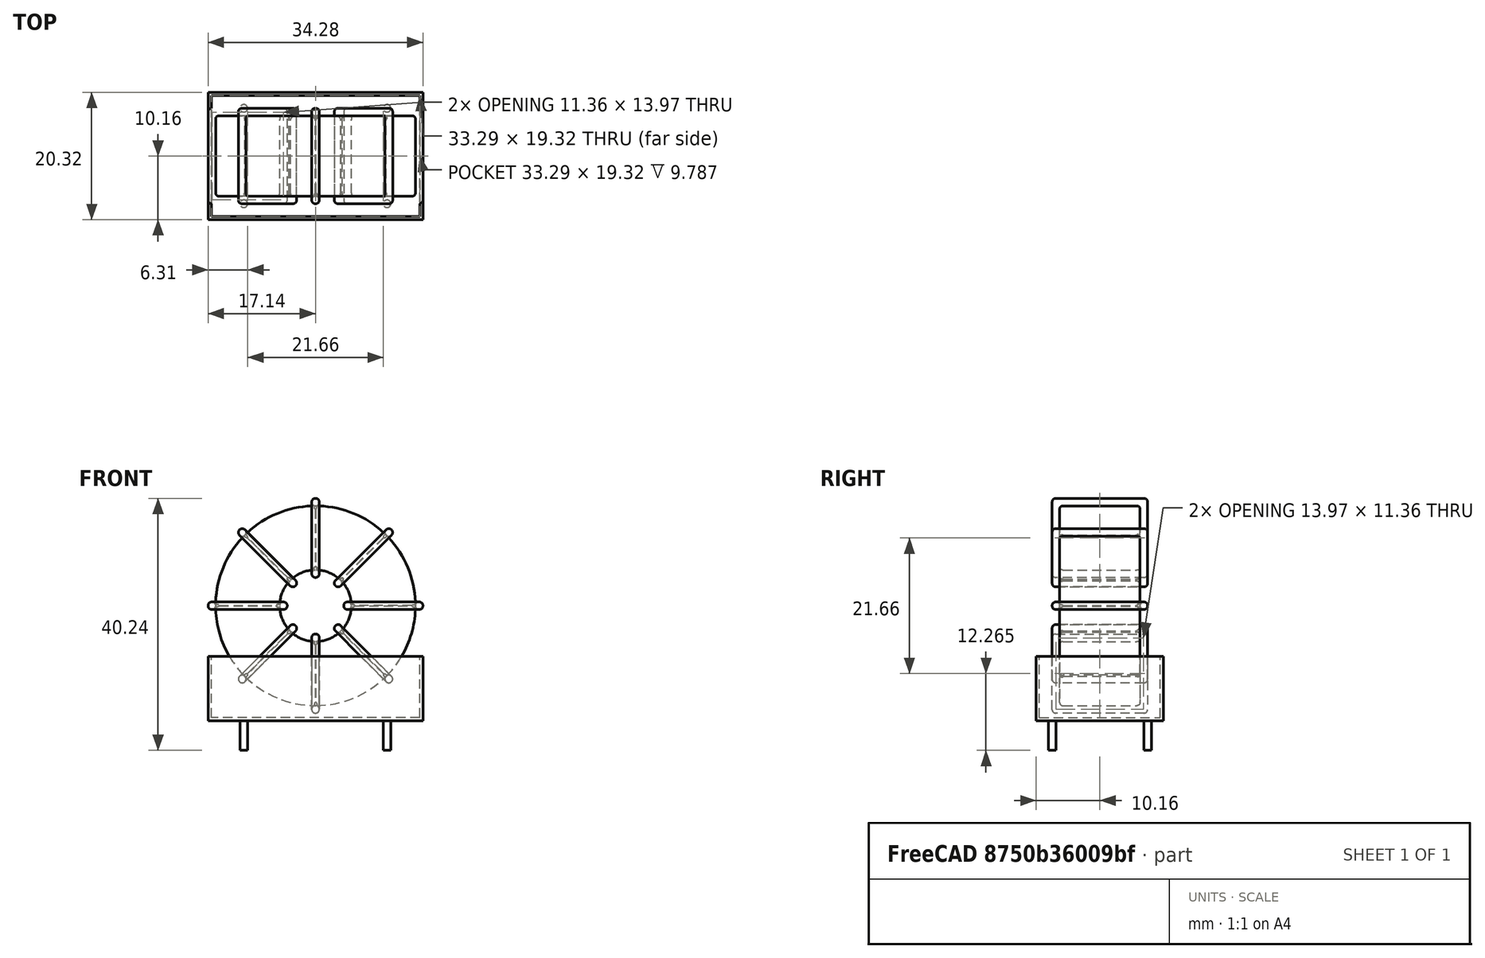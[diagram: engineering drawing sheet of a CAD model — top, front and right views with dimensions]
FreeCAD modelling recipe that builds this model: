
FCSTD DOCUMENT  (FreeCAD 0.16R6712 (Git))
Label: L_CommonMode_Toroid_Vertical_L34.3mm_W20.3mm_Px15.24mm_Py22.86mm_Bourns_8100
License: All rights reserved
LicenseURL: http://en.wikipedia.org/wiki/All_rights_reserved
objects: Sketcher::SketchObject×8, PartDesign::Pad×8, PartDesign::Fillet×5, Spreadsheet::Sheet×1, Part::MultiFuse×1
note: 30 computed .brp shape members not serialized (recipe doc carries the construction recipe); baked Part::Feature solids carry a one-line shape summary decoded from their .brp

FEATURE [Spreadsheet::Sheet] Spreadsheet  label="dimensions"
  cells = A1=Wx; B1(Wx)=34.29; C1(WW)=11.43; D1(iWx)=34.29; A2=Wy; B2(Wy)=15.24; D2(iWy)=20.32; A3=RM; B3(RMx)=15.24; C3(RMy)=22.86; A4=d_wire; B4(d_wire)=1.2; A5=H; B5(H)=31; A6=offsetx; B6(offsetx)=5.715
FEATURE [Sketcher::SketchObject] Sketch
  Placement = pos=(11.43,-7.62,0) rot=(1,0,0;1.5708rad)
  expr: Placement.Base.x = Spreadsheet.RMy / 2
  expr: Constraints[4] = Spreadsheet.WW / 2
  expr: Placement.Base.y = -Spreadsheet.RMx / 2
  expr: Constraints[0] = Spreadsheet.Wx / 2 - Spreadsheet.d_wire
  expr: Constraints[2] = Spreadsheet.Wx / 2 + Spreadsheet.d_wire + 0.5
  sketch-geometry (2):
    g0: Circle CenterX=0 CenterY=18.845 CenterZ=0 NormalX=0 NormalY=0 NormalZ=1 Radius=15.945
    g1: Circle CenterX=0 CenterY=18.845 CenterZ=0 NormalX=0 NormalY=0 NormalZ=1 Radius=5.715
  constraints (5):
    c: Radius(g0) = 15.945
    c: DistanceX(g-1,g0) = 0
    c: DistanceY(g-1,g0) = 18.845
    c: Coincident(g1,g0)
    c: Radius(g1) = 5.715
FEATURE [PartDesign::Pad] Pad
  Length = 12.84
  Length2 = 100
  Midplane = true
  Placement = pos=(11.43,-7.62,0) rot=(1,0,0;1.5708rad)
  Sketch = -> Sketch
  Type = 0
  expr: Length = Spreadsheet.Wy - 2 * Spreadsheet.d_wire
FEATURE [Sketcher::SketchObject] Sketch001
  Placement = pos=(0,0,0.75) rot=(0,0,1;0rad)
  expr: Constraints[4] = Spreadsheet.RMy
  expr: Constraints[2] = -Spreadsheet.RMx
  expr: Constraints[1] = Spreadsheet.d_wire / 2
  sketch-geometry (4):
    g0: Circle CenterX=0 CenterY=0 CenterZ=0 NormalX=0 NormalY=0 NormalZ=1 Radius=0.6
    g1: Circle CenterX=22.86 CenterY=-15.24 CenterZ=0 NormalX=0 NormalY=0 NormalZ=1 Radius=0.6
    g2: Circle CenterX=0 CenterY=-15.24 CenterZ=0 NormalX=0 NormalY=0 NormalZ=1 Radius=0.6
    g3: Circle CenterX=22.86 CenterY=0 CenterZ=0 NormalX=0 NormalY=0 NormalZ=1 Radius=0.6
  constraints (11):
    c: Equal(g0,g1)
    c: Radius(g0) = 0.6
    c: DistanceY(g-1,g1) = -15.24
    c: Coincident(g0,g-1)
    c: DistanceX(g-1,g1) = 22.86
    c: PointOnObject(g2,g-2)
    c: DistanceY(g-1,g3) = 0
    c: DistanceY(g2,g1) = 0
    c: DistanceX(g3,g1) = 0
    c: Equal(g3,g2)
    c: Equal(g2,g1)
FEATURE [PartDesign::Pad] Pad001
  Length = 5
  Length2 = 0
  Placement = pos=(0,0,0.75) rot=(0,0,1;0rad)
  Reversed = true
  Sketch = -> Sketch001
  Type = 0
FEATURE [PartDesign::Fillet] Fillet
  Base = -> Pad [Edge6,Edge3,Edge2]
  Placement = pos=(11.43,-7.62,0) rot=(1,0,0;1.5708rad)
  Radius = 0.5
FEATURE [Sketcher::SketchObject] Sketch003
  Placement = pos=(11.43,0,18.845) rot=(1,0,0;3.14159rad)
  expr: Placement.Base.x = Spreadsheet.RMy / 2
  expr: Constraints[18] = Spreadsheet.d_wire
  expr: Constraints[16] = Spreadsheet.d_wire
  expr: Constraints[19] = Spreadsheet.d_wire
  expr: Constraints[17] = Spreadsheet.d_wire
  expr: Placement.Base.y = -1 * (Spreadsheet.RMx - Spreadsheet.Wy) / 2
  expr: Constraints[21] = (Spreadsheet.Wx - Spreadsheet.WW) / 2 - Spreadsheet.d_wire
  expr: Constraints[22] = Spreadsheet.Wx / 2 - Spreadsheet.d_wire
  expr: Constraints[43] = Spreadsheet.d_wire
  expr: Constraints[48] = Spreadsheet.Wx - Spreadsheet.d_wire * 2
  expr: Constraints[49] = Spreadsheet.Wy
  expr: Placement.Base.z = Spreadsheet.Wx / 2 + Spreadsheet.d_wire + 0.5
  sketch-geometry (16):
    g0: LineSegment StartX=-4.515 StartY=0 StartZ=0 EndX=-17.145 EndY=0 EndZ=0
    g1: LineSegment StartX=-17.145 StartY=0 StartZ=0 EndX=-17.145 EndY=15.24 EndZ=0
    g2: LineSegment StartX=-17.145 StartY=15.24 StartZ=0 EndX=-4.515 EndY=15.24 EndZ=0
    g3: LineSegment StartX=-4.515 StartY=15.24 StartZ=0 EndX=-4.515 EndY=0 EndZ=0
    g4: LineSegment StartX=-15.945 StartY=14.04 StartZ=0 EndX=-5.715 EndY=14.04 EndZ=0
    g5: LineSegment StartX=-5.715 StartY=14.04 StartZ=0 EndX=-5.715 EndY=1.2 EndZ=0
    g6: LineSegment StartX=-5.715 StartY=1.2 StartZ=0 EndX=-15.945 EndY=1.2 EndZ=0
    g7: LineSegment StartX=-15.945 StartY=1.2 StartZ=0 EndX=-15.945 EndY=14.04 EndZ=0
    g8: LineSegment StartX=4.515 StartY=15.24 StartZ=0 EndX=17.145 EndY=15.24 EndZ=0
    g9: LineSegment StartX=17.145 StartY=15.24 StartZ=0 EndX=17.145 EndY=0 EndZ=0
    g10: LineSegment StartX=17.145 StartY=0 StartZ=0 EndX=4.515 EndY=0 EndZ=0
    g11: LineSegment StartX=4.515 StartY=0 StartZ=0 EndX=4.515 EndY=15.24 EndZ=0
    g12: LineSegment StartX=5.715 StartY=14.04 StartZ=0 EndX=15.945 EndY=14.04 EndZ=0
    g13: LineSegment StartX=15.945 StartY=14.04 StartZ=0 EndX=15.945 EndY=1.2 EndZ=0
    g14: LineSegment StartX=15.945 StartY=1.2 StartZ=0 EndX=5.715 EndY=1.2 EndZ=0
    g15: LineSegment StartX=5.715 StartY=1.2 StartZ=0 EndX=5.715 EndY=14.04 EndZ=0
  constraints (50):
    c: Horizontal(g0)
    c: Coincident(g1,g0)
    c: Vertical(g1)
    c: Coincident(g2,g1)
    c: Horizontal(g2)
    c: Coincident(g3,g2)
    c: Coincident(g3,g0)
    c: Vertical(g3)
    c: Coincident(g4,g5)
    c: Coincident(g5,g6)
    c: Coincident(g6,g7)
    c: Coincident(g7,g4)
    c: Horizontal(g4)
    c: Horizontal(g6)
    c: Vertical(g5)
    c: Vertical(g7)
    c: DistanceX(g1,g4) = 1.2
    c: DistanceY(g4,g1) = 1.2
    c: DistanceX(g5,g0) = 1.2
    c: DistanceY(g0,g5) = 1.2
    c: DistanceY(g-1,g0) = 0
    c: DistanceX(g6,g6) = 10.23
    c: DistanceX(g6,g-1) = 15.945
    c: Coincident(g8,g9)
    c: Coincident(g9,g10)
    c: Coincident(g10,g11)
    c: Coincident(g11,g8)
    c: Horizontal(g8)
    c: Horizontal(g10)
    c: Vertical(g9)
    c: Vertical(g11)
    c: Coincident(g12,g13)
    c: Coincident(g13,g14)
    c: Coincident(g14,g15)
    c: Coincident(g15,g12)
    c: Horizontal(g12)
    c: Horizontal(g14)
    c: Vertical(g13)
    c: Vertical(g15)
    c: DistanceY(g8,g2) = 0
    c: DistanceY(g10,g0) = 0
    c: DistanceY(g14,g5) = 0
    c: DistanceY(g12,g4) = 0
    c: DistanceX(g8,g12) = 1.2
    c: Equal(g8,g2)
    c: Equal(g12,g4)
    c: Equal(g9,g1)
    c: Equal(g13,g7)
    c: DistanceX(g4,g12) = 31.89
    c: DistanceY(g0,g1) = 15.24
FEATURE [PartDesign::Pad] Pad002
  Length = 1.2
  Length2 = 100
  Midplane = true
  Placement = pos=(11.43,0,18.845) rot=(1,0,0;3.14159rad)
  Sketch = -> Sketch003
  Type = 0
  expr: Length = Spreadsheet.d_wire
FEATURE [PartDesign::Fillet] Fillet001
  Base = -> Pad002 [Edge38,Edge41,Edge42,Edge43,Edge29,Edge32,Edge33,Edge34,Edge25,Edge35,Edge36,Edge13,Edge14,Edge15,Edge16,Edge17,Edge18,Edge19,Edge1,Edge2,Edge3,Edge4,Edge5,Edge6,Edge7,Edge37,Edge39,Edge40,Edge20,Edge23,Edge24,Edge21,Edge22,Edge8,Edge9,Edge10,Edge11,Edge12,Edge26,Edge27,+8 more]
  Placement = pos=(11.43,0,18.845) rot=(1,0,0;3.14159rad)
  Radius = 0.564
  expr: Radius = Spreadsheet.d_wire * 0.47
FEATURE [Sketcher::SketchObject] Sketch004
  Placement = pos=(11.43,0,18.845) rot=(0.92388,0,0.382683;3.14159rad)
  expr: Placement.Base.x = Spreadsheet.RMy / 2
  expr: Constraints[18] = Spreadsheet.d_wire
  expr: Constraints[16] = Spreadsheet.d_wire
  expr: Constraints[19] = Spreadsheet.d_wire
  expr: Constraints[17] = Spreadsheet.d_wire
  expr: Placement.Base.y = -1 * (Spreadsheet.RMx - Spreadsheet.Wy) / 2
  expr: Constraints[21] = (Spreadsheet.Wx - Spreadsheet.WW) / 2 - Spreadsheet.d_wire
  expr: Constraints[22] = Spreadsheet.Wx / 2 - Spreadsheet.d_wire
  expr: Constraints[43] = Spreadsheet.d_wire
  expr: Constraints[48] = Spreadsheet.Wx - 2 * Spreadsheet.d_wire
  expr: Constraints[49] = Spreadsheet.Wy
  expr: Placement.Base.z = Spreadsheet.Wx / 2 + Spreadsheet.d_wire + 0.5
  sketch-geometry (16):
    g0: LineSegment StartX=-4.515 StartY=0 StartZ=0 EndX=-17.145 EndY=0 EndZ=0
    g1: LineSegment StartX=-17.145 StartY=0 StartZ=0 EndX=-17.145 EndY=15.24 EndZ=0
    g2: LineSegment StartX=-17.145 StartY=15.24 StartZ=0 EndX=-4.515 EndY=15.24 EndZ=0
    g3: LineSegment StartX=-4.515 StartY=15.24 StartZ=0 EndX=-4.515 EndY=0 EndZ=0
    g4: LineSegment StartX=-15.945 StartY=14.04 StartZ=0 EndX=-5.715 EndY=14.04 EndZ=0
    g5: LineSegment StartX=-5.715 StartY=14.04 StartZ=0 EndX=-5.715 EndY=1.2 EndZ=0
    g6: LineSegment StartX=-5.715 StartY=1.2 StartZ=0 EndX=-15.945 EndY=1.2 EndZ=0
    g7: LineSegment StartX=-15.945 StartY=1.2 StartZ=0 EndX=-15.945 EndY=14.04 EndZ=0
    g8: LineSegment StartX=4.515 StartY=15.24 StartZ=0 EndX=17.145 EndY=15.24 EndZ=0
    g9: LineSegment StartX=17.145 StartY=15.24 StartZ=0 EndX=17.145 EndY=0 EndZ=0
    g10: LineSegment StartX=17.145 StartY=0 StartZ=0 EndX=4.515 EndY=0 EndZ=0
    g11: LineSegment StartX=4.515 StartY=0 StartZ=0 EndX=4.515 EndY=15.24 EndZ=0
    g12: LineSegment StartX=5.715 StartY=14.04 StartZ=0 EndX=15.945 EndY=14.04 EndZ=0
    g13: LineSegment StartX=15.945 StartY=14.04 StartZ=0 EndX=15.945 EndY=1.2 EndZ=0
    g14: LineSegment StartX=15.945 StartY=1.2 StartZ=0 EndX=5.715 EndY=1.2 EndZ=0
    g15: LineSegment StartX=5.715 StartY=1.2 StartZ=0 EndX=5.715 EndY=14.04 EndZ=0
  constraints (50):
    c: Horizontal(g0)
    c: Coincident(g1,g0)
    c: Vertical(g1)
    c: Coincident(g2,g1)
    c: Horizontal(g2)
    c: Coincident(g3,g2)
    c: Coincident(g3,g0)
    c: Vertical(g3)
    c: Coincident(g4,g5)
    c: Coincident(g5,g6)
    c: Coincident(g6,g7)
    c: Coincident(g7,g4)
    c: Horizontal(g4)
    c: Horizontal(g6)
    c: Vertical(g5)
    c: Vertical(g7)
    c: DistanceX(g1,g4) = 1.2
    c: DistanceY(g4,g1) = 1.2
    c: DistanceX(g5,g0) = 1.2
    c: DistanceY(g0,g5) = 1.2
    c: DistanceY(g-1,g0) = 0
    c: DistanceX(g6,g6) = 10.23
    c: DistanceX(g6,g-1) = 15.945
    c: Coincident(g8,g9)
    c: Coincident(g9,g10)
    c: Coincident(g10,g11)
    c: Coincident(g11,g8)
    c: Horizontal(g8)
    c: Horizontal(g10)
    c: Vertical(g9)
    c: Vertical(g11)
    c: Coincident(g12,g13)
    c: Coincident(g13,g14)
    c: Coincident(g14,g15)
    c: Coincident(g15,g12)
    c: Horizontal(g12)
    c: Horizontal(g14)
    c: Vertical(g13)
    c: Vertical(g15)
    c: DistanceY(g8,g2) = 0
    c: DistanceY(g10,g0) = 0
    c: DistanceY(g14,g5) = 0
    c: DistanceY(g12,g4) = 0
    c: DistanceX(g8,g12) = 1.2
    c: Equal(g8,g2)
    c: Equal(g12,g4)
    c: Equal(g9,g1)
    c: Equal(g13,g7)
    c: DistanceX(g4,g12) = 31.89
    c: DistanceY(g0,g1) = 15.24
FEATURE [PartDesign::Pad] Pad003
  Length = 1.2
  Length2 = 100
  Midplane = true
  Placement = pos=(11.43,0,18.845) rot=(0.92388,0,0.382683;3.14159rad)
  Sketch = -> Sketch004
  Type = 0
  expr: Length = Spreadsheet.d_wire
FEATURE [PartDesign::Fillet] Fillet002
  Base = -> Pad003 [Edge38,Edge41,Edge42,Edge43,Edge29,Edge32,Edge33,Edge34,Edge25,Edge35,Edge36,Edge13,Edge14,Edge15,Edge16,Edge17,Edge18,Edge19,Edge1,Edge2,Edge3,Edge4,Edge5,Edge6,Edge7,Edge37,Edge39,Edge40,Edge20,Edge23,Edge24,Edge21,Edge22,Edge8,Edge9,Edge10,Edge11,Edge12,Edge26,Edge27,+8 more]
  Placement = pos=(11.43,0,18.845) rot=(0.92388,0,0.382683;3.14159rad)
  Radius = 0.564
  expr: Radius = Spreadsheet.d_wire * 0.47
FEATURE [Sketcher::SketchObject] Sketch005
  Placement = pos=(11.43,0,18.845) rot=(0.92388,0,-0.382683;3.14159rad)
  expr: Placement.Base.x = Spreadsheet.RMy / 2
  expr: Constraints[18] = Spreadsheet.d_wire
  expr: Constraints[16] = Spreadsheet.d_wire
  expr: Constraints[19] = Spreadsheet.d_wire
  expr: Constraints[17] = Spreadsheet.d_wire
  expr: Placement.Base.y = -1 * (Spreadsheet.RMx - Spreadsheet.Wy) / 2
  expr: Constraints[21] = (Spreadsheet.Wx - Spreadsheet.WW) / 2 - Spreadsheet.d_wire
  expr: Constraints[22] = Spreadsheet.Wx / 2 - Spreadsheet.d_wire
  expr: Constraints[43] = Spreadsheet.d_wire
  expr: Constraints[48] = Spreadsheet.Wx - 2 * Spreadsheet.d_wire
  expr: Constraints[49] = Spreadsheet.Wy
  expr: Placement.Base.z = Spreadsheet.Wx / 2 + Spreadsheet.d_wire + 0.5
  sketch-geometry (16):
    g0: LineSegment StartX=-4.515 StartY=0 StartZ=0 EndX=-17.145 EndY=0 EndZ=0
    g1: LineSegment StartX=-17.145 StartY=0 StartZ=0 EndX=-17.145 EndY=15.24 EndZ=0
    g2: LineSegment StartX=-17.145 StartY=15.24 StartZ=0 EndX=-4.515 EndY=15.24 EndZ=0
    g3: LineSegment StartX=-4.515 StartY=15.24 StartZ=0 EndX=-4.515 EndY=0 EndZ=0
    g4: LineSegment StartX=-15.945 StartY=14.04 StartZ=0 EndX=-5.715 EndY=14.04 EndZ=0
    g5: LineSegment StartX=-5.715 StartY=14.04 StartZ=0 EndX=-5.715 EndY=1.2 EndZ=0
    g6: LineSegment StartX=-5.715 StartY=1.2 StartZ=0 EndX=-15.945 EndY=1.2 EndZ=0
    g7: LineSegment StartX=-15.945 StartY=1.2 StartZ=0 EndX=-15.945 EndY=14.04 EndZ=0
    g8: LineSegment StartX=4.515 StartY=15.24 StartZ=0 EndX=17.145 EndY=15.24 EndZ=0
    g9: LineSegment StartX=17.145 StartY=15.24 StartZ=0 EndX=17.145 EndY=0 EndZ=0
    g10: LineSegment StartX=17.145 StartY=0 StartZ=0 EndX=4.515 EndY=0 EndZ=0
    g11: LineSegment StartX=4.515 StartY=0 StartZ=0 EndX=4.515 EndY=15.24 EndZ=0
    g12: LineSegment StartX=5.715 StartY=14.04 StartZ=0 EndX=15.945 EndY=14.04 EndZ=0
    g13: LineSegment StartX=15.945 StartY=14.04 StartZ=0 EndX=15.945 EndY=1.2 EndZ=0
    g14: LineSegment StartX=15.945 StartY=1.2 StartZ=0 EndX=5.715 EndY=1.2 EndZ=0
    g15: LineSegment StartX=5.715 StartY=1.2 StartZ=0 EndX=5.715 EndY=14.04 EndZ=0
  constraints (50):
    c: Horizontal(g0)
    c: Coincident(g1,g0)
    c: Vertical(g1)
    c: Coincident(g2,g1)
    c: Horizontal(g2)
    c: Coincident(g3,g2)
    c: Coincident(g3,g0)
    c: Vertical(g3)
    c: Coincident(g4,g5)
    c: Coincident(g5,g6)
    c: Coincident(g6,g7)
    c: Coincident(g7,g4)
    c: Horizontal(g4)
    c: Horizontal(g6)
    c: Vertical(g5)
    c: Vertical(g7)
    c: DistanceX(g1,g4) = 1.2
    c: DistanceY(g4,g1) = 1.2
    c: DistanceX(g5,g0) = 1.2
    c: DistanceY(g0,g5) = 1.2
    c: DistanceY(g-1,g0) = 0
    c: DistanceX(g6,g6) = 10.23
    c: DistanceX(g6,g-1) = 15.945
    c: Coincident(g8,g9)
    c: Coincident(g9,g10)
    c: Coincident(g10,g11)
    c: Coincident(g11,g8)
    c: Horizontal(g8)
    c: Horizontal(g10)
    c: Vertical(g9)
    c: Vertical(g11)
    c: Coincident(g12,g13)
    c: Coincident(g13,g14)
    c: Coincident(g14,g15)
    c: Coincident(g15,g12)
    c: Horizontal(g12)
    c: Horizontal(g14)
    c: Vertical(g13)
    c: Vertical(g15)
    c: DistanceY(g8,g2) = 0
    c: DistanceY(g10,g0) = 0
    c: DistanceY(g14,g5) = 0
    c: DistanceY(g12,g4) = 0
    c: DistanceX(g8,g12) = 1.2
    c: Equal(g8,g2)
    c: Equal(g12,g4)
    c: Equal(g9,g1)
    c: Equal(g13,g7)
    c: DistanceX(g4,g12) = 31.89
    c: DistanceY(g0,g1) = 15.24
FEATURE [PartDesign::Pad] Pad004
  Length = 1.2
  Length2 = 100
  Midplane = true
  Placement = pos=(11.43,0,18.845) rot=(0.92388,0,-0.382683;3.14159rad)
  Sketch = -> Sketch005
  Type = 0
  expr: Length = Spreadsheet.d_wire
FEATURE [PartDesign::Fillet] Fillet003
  Base = -> Pad004 [Edge38,Edge41,Edge42,Edge43,Edge29,Edge32,Edge33,Edge34,Edge25,Edge35,Edge36,Edge13,Edge14,Edge15,Edge16,Edge17,Edge18,Edge19,Edge1,Edge2,Edge3,Edge4,Edge5,Edge6,Edge7,Edge37,Edge39,Edge40,Edge20,Edge23,Edge24,Edge21,Edge22,Edge8,Edge9,Edge10,Edge11,Edge12,Edge26,Edge27,+8 more]
  Placement = pos=(11.43,0,18.845) rot=(0.92388,0,-0.382683;3.14159rad)
  Radius = 0.564
  expr: Radius = Spreadsheet.d_wire * 0.47
FEATURE [Sketcher::SketchObject] Sketch006
  Placement = pos=(11.43,0,18.845) rot=(0.707107,0,0.707107;3.14159rad)
  expr: Placement.Base.x = Spreadsheet.RMy / 2
  expr: Constraints[18] = Spreadsheet.d_wire
  expr: Constraints[16] = Spreadsheet.d_wire
  expr: Constraints[19] = Spreadsheet.d_wire
  expr: Constraints[17] = Spreadsheet.d_wire
  expr: Placement.Base.y = -1 * (Spreadsheet.RMx - Spreadsheet.Wy) / 2
  expr: Constraints[21] = (Spreadsheet.Wx - Spreadsheet.WW) / 2 - Spreadsheet.d_wire
  expr: Constraints[22] = Spreadsheet.Wx / 2 - Spreadsheet.d_wire
  expr: Constraints[43] = Spreadsheet.d_wire
  expr: Constraints[48] = Spreadsheet.Wx - Spreadsheet.d_wire * 2
  expr: Constraints[49] = Spreadsheet.Wy
  expr: Placement.Base.z = Spreadsheet.Wx / 2 + Spreadsheet.d_wire + 0.5
  sketch-geometry (16):
    g0: LineSegment StartX=-4.515 StartY=0 StartZ=0 EndX=-17.145 EndY=0 EndZ=0
    g1: LineSegment StartX=-17.145 StartY=0 StartZ=0 EndX=-17.145 EndY=15.24 EndZ=0
    g2: LineSegment StartX=-17.145 StartY=15.24 StartZ=0 EndX=-4.515 EndY=15.24 EndZ=0
    g3: LineSegment StartX=-4.515 StartY=15.24 StartZ=0 EndX=-4.515 EndY=0 EndZ=0
    g4: LineSegment StartX=-15.945 StartY=14.04 StartZ=0 EndX=-5.715 EndY=14.04 EndZ=0
    g5: LineSegment StartX=-5.715 StartY=14.04 StartZ=0 EndX=-5.715 EndY=1.2 EndZ=0
    g6: LineSegment StartX=-5.715 StartY=1.2 StartZ=0 EndX=-15.945 EndY=1.2 EndZ=0
    g7: LineSegment StartX=-15.945 StartY=1.2 StartZ=0 EndX=-15.945 EndY=14.04 EndZ=0
    g8: LineSegment StartX=4.515 StartY=15.24 StartZ=0 EndX=17.145 EndY=15.24 EndZ=0
    g9: LineSegment StartX=17.145 StartY=15.24 StartZ=0 EndX=17.145 EndY=0 EndZ=0
    g10: LineSegment StartX=17.145 StartY=0 StartZ=0 EndX=4.515 EndY=0 EndZ=0
    g11: LineSegment StartX=4.515 StartY=0 StartZ=0 EndX=4.515 EndY=15.24 EndZ=0
    g12: LineSegment StartX=5.715 StartY=14.04 StartZ=0 EndX=15.945 EndY=14.04 EndZ=0
    g13: LineSegment StartX=15.945 StartY=14.04 StartZ=0 EndX=15.945 EndY=1.2 EndZ=0
    g14: LineSegment StartX=15.945 StartY=1.2 StartZ=0 EndX=5.715 EndY=1.2 EndZ=0
    g15: LineSegment StartX=5.715 StartY=1.2 StartZ=0 EndX=5.715 EndY=14.04 EndZ=0
  constraints (50):
    c: Horizontal(g0)
    c: Coincident(g1,g0)
    c: Vertical(g1)
    c: Coincident(g2,g1)
    c: Horizontal(g2)
    c: Coincident(g3,g2)
    c: Coincident(g3,g0)
    c: Vertical(g3)
    c: Coincident(g4,g5)
    c: Coincident(g5,g6)
    c: Coincident(g6,g7)
    c: Coincident(g7,g4)
    c: Horizontal(g4)
    c: Horizontal(g6)
    c: Vertical(g5)
    c: Vertical(g7)
    c: DistanceX(g1,g4) = 1.2
    c: DistanceY(g4,g1) = 1.2
    c: DistanceX(g5,g0) = 1.2
    c: DistanceY(g0,g5) = 1.2
    c: DistanceY(g-1,g0) = 0
    c: DistanceX(g6,g6) = 10.23
    c: DistanceX(g6,g-1) = 15.945
    c: Coincident(g8,g9)
    c: Coincident(g9,g10)
    c: Coincident(g10,g11)
    c: Coincident(g11,g8)
    c: Horizontal(g8)
    c: Horizontal(g10)
    c: Vertical(g9)
    c: Vertical(g11)
    c: Coincident(g12,g13)
    c: Coincident(g13,g14)
    c: Coincident(g14,g15)
    c: Coincident(g15,g12)
    c: Horizontal(g12)
    c: Horizontal(g14)
    c: Vertical(g13)
    c: Vertical(g15)
    c: DistanceY(g8,g2) = 0
    c: DistanceY(g10,g0) = 0
    c: DistanceY(g14,g5) = 0
    c: DistanceY(g12,g4) = 0
    c: DistanceX(g8,g12) = 1.2
    c: Equal(g8,g2)
    c: Equal(g12,g4)
    c: Equal(g9,g1)
    c: Equal(g13,g7)
    c: DistanceX(g4,g12) = 31.89
    c: DistanceY(g0,g1) = 15.24
FEATURE [PartDesign::Pad] Pad005
  Length = 1.2
  Length2 = 100
  Midplane = true
  Placement = pos=(11.43,0,18.845) rot=(0.707107,0,0.707107;3.14159rad)
  Sketch = -> Sketch006
  Type = 0
  expr: Length = Spreadsheet.d_wire
FEATURE [PartDesign::Fillet] Fillet004
  Base = -> Pad005 [Edge38,Edge41,Edge42,Edge43,Edge29,Edge32,Edge33,Edge34,Edge25,Edge35,Edge36,Edge13,Edge14,Edge15,Edge16,Edge17,Edge18,Edge19,Edge1,Edge2,Edge3,Edge4,Edge5,Edge6,Edge7,Edge37,Edge39,Edge40,Edge20,Edge23,Edge24,Edge21,Edge22,Edge8,Edge9,Edge10,Edge11,Edge12,Edge26,Edge27,+8 more]
  Placement = pos=(11.43,0,18.845) rot=(0.707107,0,0.707107;3.14159rad)
  Radius = 0.564
  expr: Radius = Spreadsheet.d_wire * 0.47
FEATURE [Sketcher::SketchObject] Sketch007
  Placement = pos=(11.43,0,0.5) rot=(0,0,1;0rad)
  expr: Placement.Base.x = Spreadsheet.RMy / 2
  expr: Placement.Base.z = 0.5
  expr: Constraints[11] = Spreadsheet.iWx / 2
  expr: Constraints[10] = (Spreadsheet.iWy - Spreadsheet.RMx) / 2
  expr: Constraints[9] = Spreadsheet.iWy
  expr: Constraints[8] = Spreadsheet.iWx
  sketch-geometry (4):
    g0: LineSegment StartX=-17.145 StartY=2.54 StartZ=0 EndX=17.145 EndY=2.54 EndZ=0
    g1: LineSegment StartX=17.145 StartY=2.54 StartZ=0 EndX=17.145 EndY=-17.78 EndZ=0
    g2: LineSegment StartX=17.145 StartY=-17.78 StartZ=0 EndX=-17.145 EndY=-17.78 EndZ=0
    g3: LineSegment StartX=-17.145 StartY=-17.78 StartZ=0 EndX=-17.145 EndY=2.54 EndZ=0
  constraints (12):
    c: Coincident(g0,g1)
    c: Coincident(g1,g2)
    c: Coincident(g2,g3)
    c: Coincident(g3,g0)
    c: Horizontal(g0)
    c: Horizontal(g2)
    c: Vertical(g1)
    c: Vertical(g3)
    c: DistanceX(g0,g0) = 34.29
    c: DistanceY(g3,g3) = 20.32
    c: DistanceY(g-1,g0) = 2.54
    c: DistanceX(g0,g-1) = 17.145
FEATURE [PartDesign::Pad] Pad006
  Length = 0.5
  Length2 = 100
  Placement = pos=(11.43,0,0.5) rot=(0,0,1;0rad)
  Sketch = -> Sketch007
  Type = 0
FEATURE [Sketcher::SketchObject] Sketch008
  Placement = pos=(11.43,0,0.5) rot=(0,0,1;0rad)
  expr: Placement.Base.x = Spreadsheet.RMy / 2
  expr: Constraints[8] = Spreadsheet.iWx
  expr: Constraints[9] = Spreadsheet.iWy
  expr: Constraints[10] = (Spreadsheet.iWy - Spreadsheet.RMx) / 2
  expr: Placement.Base.z = 0.5
  expr: Constraints[21] = 0.5
  expr: Constraints[11] = Spreadsheet.iWx / 2
  sketch-geometry (8):
    g0: LineSegment StartX=-17.145 StartY=2.54 StartZ=0 EndX=17.145 EndY=2.54 EndZ=0
    g1: LineSegment StartX=17.145 StartY=2.54 StartZ=0 EndX=17.145 EndY=-17.78 EndZ=0
    g2: LineSegment StartX=17.145 StartY=-17.78 StartZ=0 EndX=-17.145 EndY=-17.78 EndZ=0
    g3: LineSegment StartX=-17.145 StartY=-17.78 StartZ=0 EndX=-17.145 EndY=2.54 EndZ=0
    g4: LineSegment StartX=-16.645 StartY=2.04 StartZ=0 EndX=16.645 EndY=2.04 EndZ=0
    g5: LineSegment StartX=16.645 StartY=2.04 StartZ=0 EndX=16.645 EndY=-17.28 EndZ=0
    g6: LineSegment StartX=16.645 StartY=-17.28 StartZ=0 EndX=-16.645 EndY=-17.28 EndZ=0
    g7: LineSegment StartX=-16.645 StartY=-17.28 StartZ=0 EndX=-16.645 EndY=2.04 EndZ=0
  constraints (24):
    c: Coincident(g0,g1)
    c: Coincident(g1,g2)
    c: Coincident(g2,g3)
    c: Coincident(g3,g0)
    c: Horizontal(g0)
    c: Horizontal(g2)
    c: Vertical(g1)
    c: Vertical(g3)
    c: DistanceX(g0,g0) = 34.29
    c: DistanceY(g3,g3) = 20.32
    c: DistanceY(g-1,g0) = 2.54
    c: DistanceX(g0,g-1) = 17.145
    c: Coincident(g4,g5)
    c: Coincident(g5,g6)
    c: Coincident(g6,g7)
    c: Coincident(g7,g4)
    c: Horizontal(g4)
    c: Horizontal(g6)
    c: Vertical(g5)
    c: Vertical(g7)
    c: DistanceX(g5,g1) = 0.5
    c: DistanceY(g1,g5) = 0.5
    c: DistanceX(g0,g4) = 0.5
    c: DistanceY(g4,g0) = 0.5
FEATURE [PartDesign::Pad] Pad007
  Length = 10.287
  Length2 = 100
  Placement = pos=(11.43,0,0.5) rot=(0,0,1;0rad)
  Sketch = -> Sketch008
  Type = 0
  expr: Length = Spreadsheet.Wx * 0.3
FEATURE [Part::MultiFuse] Pad001_mp_cp  label="L_CommonMode_Toroid_Vertical_L34.3mm_W20.3mm_Px15.24mm_Py22.86mm_Bourns_8100"
  Shapes = -> [Pad001,Fillet,Fillet001,Fillet002,Fillet003,Fillet004,Pad006,Pad007]
